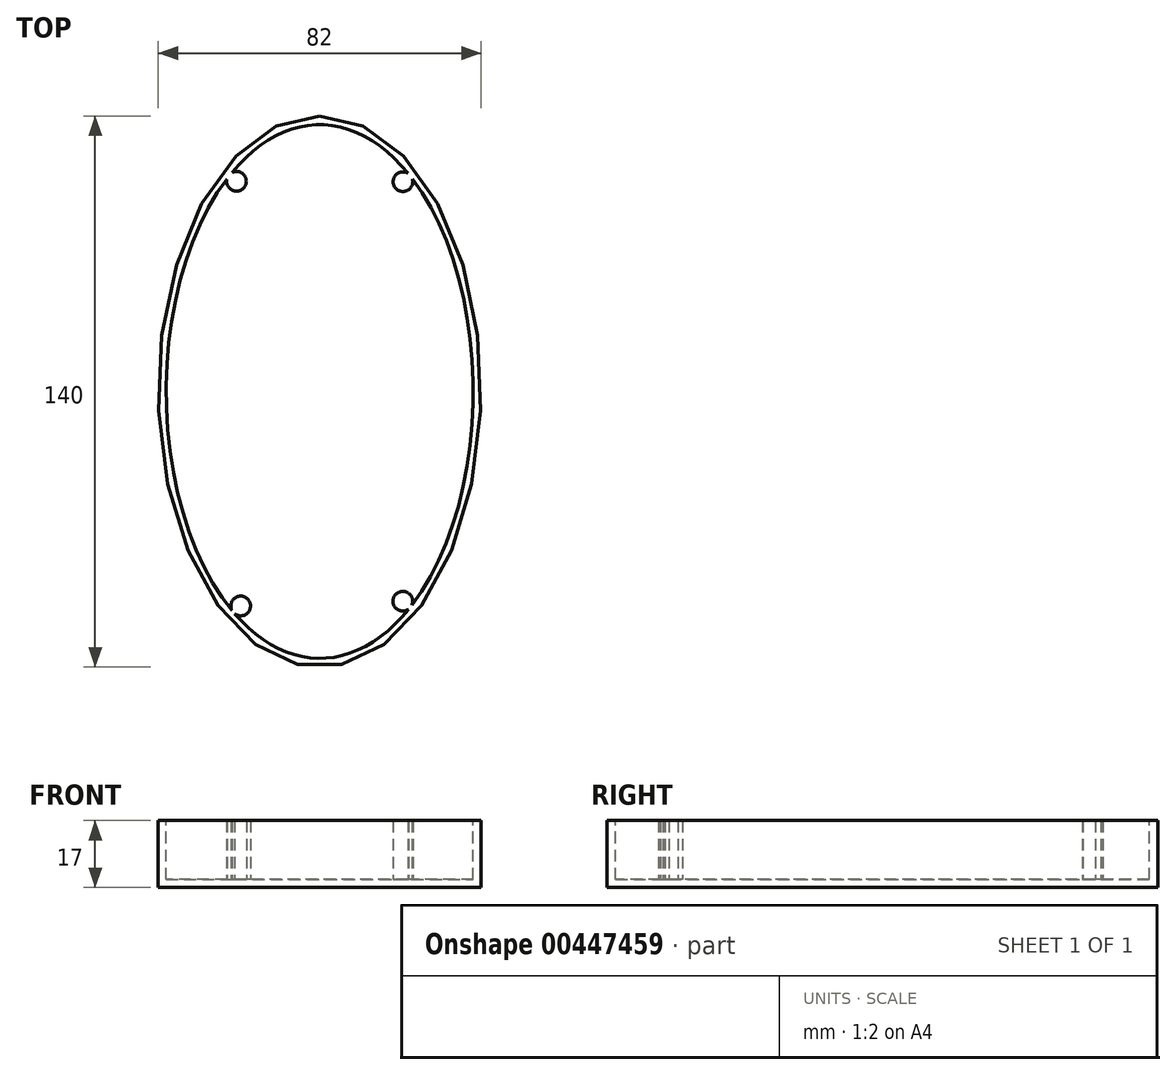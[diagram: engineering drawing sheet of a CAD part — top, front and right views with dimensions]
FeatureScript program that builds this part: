
annotation { "Feature Type Name" : "Feature", "Feature Type Description" : "" }
export const myFeature = defineFeature(function(context is Context, id is Id, definition is map)
    precondition{}
    {
        {
            var Q0;
            Q0=qCreatedBy(makeId("Top.planeOp"),FACE);
            var sketch = newSketch(context, id + "F0", { "sketchPlane" : qUnion([Q0])});
            skEllipse(sketch, "E0", {"center": v(-6.22, 3.26) * mm, "majorRadius": 70 * mm, "minorRadius": 41 * mm, "majorAxis": v(0, 1)});
            skSolve(sketch);
        }
        {
            var Q0;
            Q0 = qSketchRegion(id + "F0", true);
            extrude(context, id + "F1", {"entities" : qUnion([Q0]), "depth" : 17 * mm});
        }
        {
            var Q0;
            Q0=makeQuery(id+"F1.opExtrude","CAP_FACE",FACE,{"disambiguationData":[OSD([sQuery(id+"F0.wireOp",EDGE,"E0")])],"isStart":false});
            var sketch = newSketch(context, id + "F2", { "sketchPlane" : qUnion([Q0])});
            skEllipse(sketch, "E1", {"center": v(-6.22, 3.26) * mm, "majorRadius": 67.8 * mm, "minorRadius": 39 * mm, "majorAxis": v(0, 1)});
            skSolve(sketch);
        }
        {
            var Q0;
            Q0=makeQuery(id+"F2.imprint","IMPRINT",FACE,{"disambiguationData":[TD([[makeQuery(id+"F2.imprint","IMPRINT",EDGE,{"derivedFrom":sQuery(id+"F2.wireOp",EDGE,"E1")}),1.0]])]});
            extrude(context, id + "F3", {"entities" : qUnion([Q0]), "operationType" : NewBodyOperationType.REMOVE, "oppositeDirection" : true, "depth" : 15 * mm});
        }
        {
            var Q0;
            Q0=makeQuery(id+"F3.boolean.opBoolean","COPY",FACE,{"derivedFrom":makeQuery(id+"F3.opExtrude","CAP_FACE",FACE,{"disambiguationData":[OSD([sQuery(id+"F2.wireOp",EDGE,"E1")])],"isStart":false})});
            var sketch = newSketch(context, id + "F4", { "sketchPlane" : qUnion([Q0])});
            skCircle(sketch, "E2", {"center": v(-27.35, 56.69) * mm, "radius": 2.5 * mm});
            skPoint(sketch, "E2.first.point", {"position": v(-28.49, 58.91) * mm});
            skPoint(sketch, "E2.second.point", {"position": v(-26.1, 54.53) * mm});
            skPoint(sketch, "E2.third.point", {"position": v(-27.44, 54.19) * mm});
            skSolve(sketch);
        }
        {
            var Q0;
            {var subQ0=sQuery(id+"F4.wireOp",EDGE,"E2");var subQ1=makeQuery(id+"F3.boolean.opBoolean","COPY",EDGE,{"derivedFrom":makeQuery(id+"F3.opExtrude","CAP_EDGE",EDGE,{"disambiguationData":[OSD([sQuery(id+"F2.wireOp",EDGE,"E1")])],"isStart":false})});var subQ2=makeQuery(id+"F4.imprint","INTERSECT",VERTEX,{"disambiguationData":[OD(0.0)],"derivedFrom":[subQ1,subQ0]});Q0=makeQuery(id+"F4.imprint","IMPRINT",FACE,{"disambiguationData":[TD([[makeQuery(id+"F4.imprint","IMPRINT",EDGE,{"disambiguationData":[TD([[subQ2,-1.0]])],"derivedFrom":subQ0}),1.0]])]});}
            extrude(context, id + "F5", {"entities" : qUnion([Q0]), "operationType" : NewBodyOperationType.ADD, "depth" : 15 * mm});
        }
        {
            var Q0;
            Q0=makeQuery(id+"F3.boolean.opBoolean","COPY",FACE,{"derivedFrom":makeQuery(id+"F3.opExtrude","CAP_FACE",FACE,{"disambiguationData":[OSD([sQuery(id+"F2.wireOp",EDGE,"E1")])],"isStart":false})});
            var sketch = newSketch(context, id + "F6", { "sketchPlane" : qUnion([Q0])});
            skCircle(sketch, "E3", {"center": v(14.94, 56.58) * mm, "radius": 2.5 * mm});
            skPoint(sketch, "E3.first.point", {"position": v(12.51, 56) * mm});
            skPoint(sketch, "E3.second.point", {"position": v(17.34, 57.29) * mm});
            skPoint(sketch, "E3.third.point", {"position": v(16.01, 54.32) * mm});
            skSolve(sketch);
        }
        {
            var Q0;
            {var subQ0=sQuery(id+"F6.wireOp",EDGE,"E3");var subQ1=makeQuery(id+"F3.boolean.opBoolean","COPY",EDGE,{"derivedFrom":makeQuery(id+"F3.opExtrude","CAP_EDGE",EDGE,{"disambiguationData":[OSD([sQuery(id+"F2.wireOp",EDGE,"E1")])],"isStart":false})});var subQ2=makeQuery(id+"F6.imprint","INTERSECT",VERTEX,{"disambiguationData":[OD(0.0)],"derivedFrom":[subQ1,subQ0]});Q0=makeQuery(id+"F6.imprint","IMPRINT",FACE,{"disambiguationData":[TD([[makeQuery(id+"F6.imprint","IMPRINT",EDGE,{"disambiguationData":[TD([[subQ2,1.0]])],"derivedFrom":subQ0}),1.0]])]});}
            extrude(context, id + "F7", {"entities" : qUnion([Q0]), "operationType" : NewBodyOperationType.ADD, "depth" : 15 * mm});
        }
        {
            var Q0;
            Q0=makeQuery(id+"F3.boolean.opBoolean","COPY",FACE,{"derivedFrom":makeQuery(id+"F3.opExtrude","CAP_FACE",FACE,{"disambiguationData":[OSD([sQuery(id+"F2.wireOp",EDGE,"E1")])],"isStart":false})});
            var sketch = newSketch(context, id + "F8", { "sketchPlane" : qUnion([Q0])});
            skCircle(sketch, "E4", {"center": v(-26.28, -51.22) * mm, "radius": 2.5 * mm});
            skPoint(sketch, "E4.first.point", {"position": v(-28.49, -50.03) * mm});
            skPoint(sketch, "E4.second.point", {"position": v(-24.98, -49.08) * mm});
            skPoint(sketch, "E4.third.point", {"position": v(-28.49, -52.4) * mm});
            skSolve(sketch);
        }
        {
            var Q0;
            {var subQ0=sQuery(id+"F8.wireOp",EDGE,"E4");var subQ1=makeQuery(id+"F7.boolean.opBoolean","SPLIT",EDGE,{"disambiguationData":[OD(0.0)],"derivedFrom":makeQuery(id+"F3.boolean.opBoolean","COPY",EDGE,{"derivedFrom":makeQuery(id+"F3.opExtrude","CAP_EDGE",EDGE,{"disambiguationData":[OSD([sQuery(id+"F2.wireOp",EDGE,"E1")])],"isStart":false})})});var subQ2=makeQuery(id+"F8.imprint","INTERSECT",VERTEX,{"disambiguationData":[OD(0.0)],"derivedFrom":[subQ1,subQ0]});Q0=makeQuery(id+"F8.imprint","IMPRINT",FACE,{"disambiguationData":[TD([[makeQuery(id+"F8.imprint","IMPRINT",EDGE,{"disambiguationData":[TD([[subQ2,1.0]])],"derivedFrom":subQ0}),1.0]])]});}
            extrude(context, id + "F9", {"entities" : qUnion([Q0]), "operationType" : NewBodyOperationType.ADD, "depth" : 15 * mm});
        }
        {
            var Q0;
            Q0=makeQuery(id+"F3.boolean.opBoolean","COPY",FACE,{"derivedFrom":makeQuery(id+"F3.opExtrude","CAP_FACE",FACE,{"disambiguationData":[OSD([sQuery(id+"F2.wireOp",EDGE,"E1")])],"isStart":false})});
            var sketch = newSketch(context, id + "F10", { "sketchPlane" : qUnion([Q0])});
            skCircle(sketch, "E5", {"center": v(14.89, -50.02) * mm, "radius": 2.5 * mm});
            skPoint(sketch, "E5.first.point", {"position": v(17.2, -50.95) * mm});
            skPoint(sketch, "E5.second.point", {"position": v(12.45, -49.45) * mm});
            skPoint(sketch, "E5.third.point", {"position": v(13.95, -47.7) * mm});
            skSolve(sketch);
        }
        {
            var Q0;
            {var subQ0=sQuery(id+"F10.wireOp",EDGE,"E5");var subQ1=sQuery(id+"F2.wireOp",EDGE,"E1");var subQ2=makeQuery(id+"F9.boolean.opBoolean","SPLIT",EDGE,{"disambiguationData":[TD([makeQuery(id+"F7.opExtrude","SWEPT_FACE",FACE,{"disambiguationData":[OSD([sQuery(id+"F6.wireOp",EDGE,"E3")])]})])],"derivedFrom":makeQuery(id+"F7.boolean.opBoolean","SPLIT",EDGE,{"disambiguationData":[OD(0.0)],"derivedFrom":makeQuery(id+"F3.boolean.opBoolean","COPY",EDGE,{"derivedFrom":makeQuery(id+"F3.opExtrude","CAP_EDGE",EDGE,{"disambiguationData":[OSD([subQ1])],"isStart":false})})})});var subQ3=makeQuery(id+"F10.imprint","INTERSECT",VERTEX,{"disambiguationData":[OD(0.0)],"derivedFrom":[subQ2,subQ0]});Q0=makeQuery(id+"F10.imprint","IMPRINT",FACE,{"disambiguationData":[TD([[makeQuery(id+"F10.imprint","IMPRINT",EDGE,{"disambiguationData":[TD([[subQ3,-1.0]])],"derivedFrom":subQ0}),1.0]])]});}
            extrude(context, id + "F11", {"entities" : qUnion([Q0]), "operationType" : NewBodyOperationType.ADD, "depth" : 15 * mm});
        }
    });
